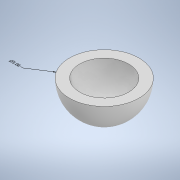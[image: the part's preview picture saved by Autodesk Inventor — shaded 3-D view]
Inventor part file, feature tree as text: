
AUTODESK INVENTOR PART (.ipt)
format: ipt  version: 2022 (Build 260153000, 153)  size: 322,560 bytes
history: native  units: in
note: dims shown in document units (in); Inventor stores cm internally (conversion verified against a paired STEP export)
features: other x2, revolve x1, thicken_offset x1, shell x1, sketch x1
ambient origin geometry x8: Origin, YZ Plane, XZ Plane, XY Plane, X Axis, Y Axis, Z Axis, Center Point
bodies: Solid1 (feature_tree)
feature tree (6):
  other  "Annotations"
  revolve  "Revolution1"  [1 undecoded]
  thicken_offset  "Thicken1"
  shell  "Shell1"  Thickness=1.03in
  sketch  "Sketch1"  dims[d3=90.0deg d6=1.03in d7=1.03in d8=0.75in d4=0.2255in d5=5.06in]
  other  "Diameter Dimension 1"
note: 1 required parameter value undecoded (feature->parameter linkage not recoverable at this tier; creation-order binding heuristic only, values carry confidence <= 0.55)
